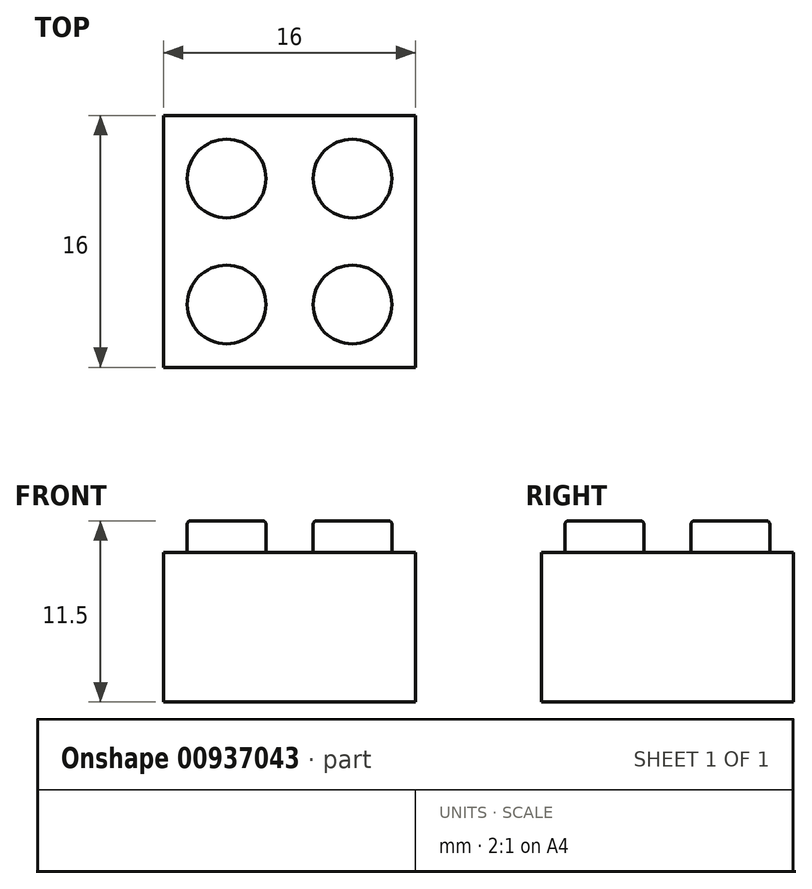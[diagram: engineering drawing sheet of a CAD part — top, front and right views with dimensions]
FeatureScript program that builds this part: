
annotation { "Feature Type Name" : "Feature", "Feature Type Description" : "" }
export const myFeature = defineFeature(function(context is Context, id is Id, definition is map)
    precondition{}
    {
        {
            var Q0;
            Q0=qCreatedBy(makeId("Front.planeOp"),FACE);
            var sketch = newSketch(context, id + "F0", { "sketchPlane" : qUnion([Q0])});
            skLineSegment(sketch, "E0.bottom", {"start": v(4, 4.75) * mm, "end": v(-4, 4.75) * mm});
            skLineSegment(sketch, "E0.top", {"start": v(4, -4.75) * mm, "end": v(-4, -4.75) * mm});
            skLineSegment(sketch, "E0.left", {"start": v(4, 4.75) * mm, "end": v(4, -4.75) * mm});
            skLineSegment(sketch, "E0.right", {"start": v(-4, 4.75) * mm, "end": v(-4, -4.75) * mm});
            skPoint(sketch, "E0.middle", {"position": v(0, 0) * mm});
            skLineSegment(sketch, "E1.bottom", {"start": v(0, 4.75) * mm, "end": v(-2.5, 4.75) * mm});
            skLineSegment(sketch, "E1.top", {"start": v(0, 6.75) * mm, "end": v(-2.5, 6.75) * mm});
            skLineSegment(sketch, "E1.left", {"start": v(0, 4.75) * mm, "end": v(0, 6.75) * mm});
            skLineSegment(sketch, "E1.right", {"start": v(-2.5, 4.75) * mm, "end": v(-2.5, 6.75) * mm});
            skSolve(sketch);
        }
        {
            var Q0;
            Q0=makeQuery(id+"F0.imprint","IMPRINT",FACE,{"disambiguationData":[TD([[makeQuery(id+"F0.imprint","IMPRINT",EDGE,{"derivedFrom":sQuery(id+"F0.wireOp",EDGE,"E1.top")}),1.0]])]});
            var Q1;
            Q1=sQuery(id+"F0.wireOp",EDGE,"E1.left");
            revolve(context, id + "F1", {"surfaceOperationType" : NewSurfaceOperationType.NEW, "entities" : qUnion([Q0]), "axis" : qUnion([Q1]), "revolveType" : RevolveType.FULL});
        }
        {
            var Q0;
            Q0=makeQuery(id+"F0.imprint","IMPRINT",FACE,{"disambiguationData":[TD([[makeQuery(id+"F0.imprint","IMPRINT",EDGE,{"derivedFrom":sQuery(id+"F0.wireOp",EDGE,"E0.top")}),-1.0]])]});
            extrude(context, id + "F2", {"entities" : qUnion([Q0]), "operationType" : NewBodyOperationType.ADD, "depth" : 8 * mm, "offsetDistance" : 25.4 * mm, "symmetric" : true});
        }
        {
            var Q0;
            Q0=makeQuery(id+"F1.opRevolve","SWEPT_EDGE",EDGE,{"disambiguationData":[OSD([sQuery(id+"F0.wireOp",EDGE,"E1.top"),sQuery(id+"F0.wireOp",EDGE,"E1.right")])]});
            fillet(context, id + "F3", {"entities" : qUnion([Q0]), "radius" : 0.2 * mm, "tangentPropagation" : true, "allowEdgeOverflow" : false});
        }
        {
            var Q0;
            Q0=makeQuery(id+"F1.opRevolve","SWEPT_BODY",BODY,{"disambiguationData":[OSD([sQuery(id+"F0.wireOp",EDGE,"E0.bottom"),sQuery(id+"F0.wireOp",EDGE,"E1.top"),sQuery(id+"F0.wireOp",EDGE,"E1.left"),sQuery(id+"F0.wireOp",EDGE,"E1.right")])]});
            var Q1;
            Q1=makeQuery(id+"F2.opExtrude","CAP_FACE",FACE,{"disambiguationData":[OSD([sQuery(id+"F0.wireOp",EDGE,"E0.bottom"),sQuery(id+"F0.wireOp",EDGE,"E0.top"),sQuery(id+"F0.wireOp",EDGE,"E0.left"),sQuery(id+"F0.wireOp",EDGE,"E0.right")])],"isStart":false});
            mirror(context, id + "F4", {"operationType" : NewBodyOperationType.ADD, "entities" : qUnion([Q0]), "mirrorPlane" : qUnion([Q1])});
        }
        {
            var Q0;
            Q0=makeQuery(id+"F1.opRevolve","SWEPT_BODY",BODY,{"disambiguationData":[OSD([sQuery(id+"F0.wireOp",EDGE,"E0.bottom"),sQuery(id+"F0.wireOp",EDGE,"E1.top"),sQuery(id+"F0.wireOp",EDGE,"E1.left"),sQuery(id+"F0.wireOp",EDGE,"E1.right")])]});
            var Q1;
            {var subQ0=makeQuery(id+"F2.opExtrude","SWEPT_FACE",FACE,{"disambiguationData":[OSD([sQuery(id+"F0.wireOp",EDGE,"E0.left")])]});Q1=makeQuery(id+"F4.boolean.opBoolean","MERGE",FACE,{"derivedFrom":[subQ0,makeQuery(id+"F4.opPattern","COPY",FACE,{"derivedFrom":subQ0,"instanceName":"1"})]});}
            mirror(context, id + "F5", {"operationType" : NewBodyOperationType.ADD, "entities" : qUnion([Q0]), "mirrorPlane" : qUnion([Q1])});
        }
        {
            var Q0;
            Q0=makeQuery(id+"F1.opRevolve","SWEPT_BODY",BODY,{"disambiguationData":[OSD([sQuery(id+"F0.wireOp",EDGE,"E0.bottom"),sQuery(id+"F0.wireOp",EDGE,"E1.top"),sQuery(id+"F0.wireOp",EDGE,"E1.left"),sQuery(id+"F0.wireOp",EDGE,"E1.right")])]});
            transform(context, id + "F6", {"entities" : qUnion([Q0]), "transformType" : TransformType.TRANSLATION_3D, "dx" : 0 * mm, "dy" : 0 * mm, "dz" : 0 * mm, "makeCopy" : true});
        }
    });
